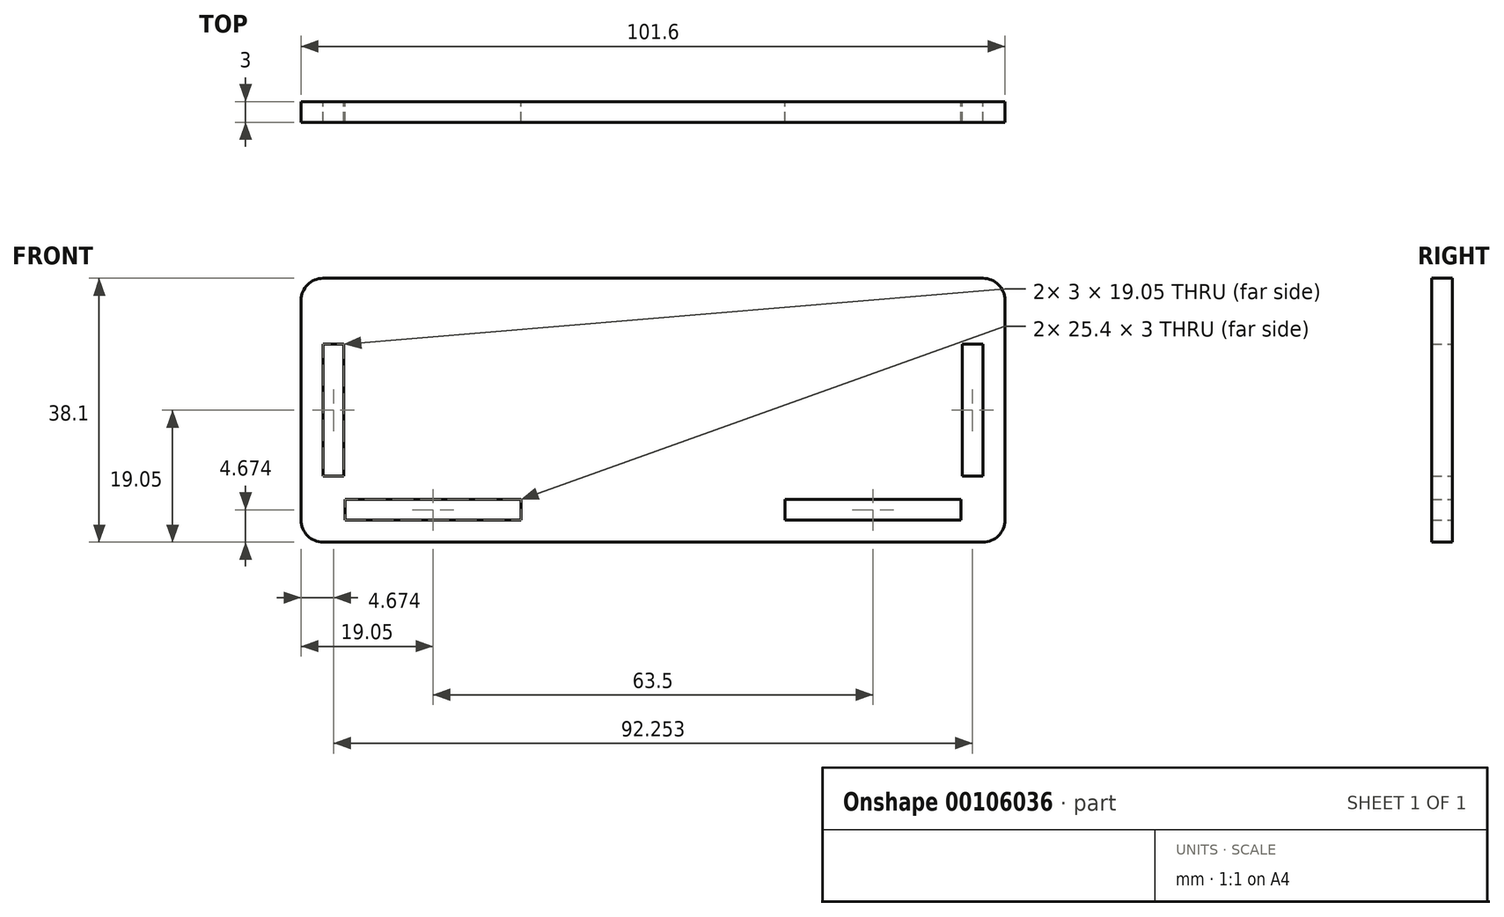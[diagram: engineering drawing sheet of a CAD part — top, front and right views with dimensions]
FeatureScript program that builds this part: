
annotation { "Feature Type Name" : "Feature", "Feature Type Description" : "" }
export const myFeature = defineFeature(function(context is Context, id is Id, definition is map)
    precondition{}
    {
        {
            var Q0;
            Q0=qCreatedBy(makeId("Front.planeOp"),FACE);
            var sketch = newSketch(context, id + "F0", { "sketchPlane" : qUnion([Q0])});
            skLineSegment(sketch, "E0.bottom", {"start": v(-47.63, 0) * mm, "end": v(47.63, 0) * mm});
            skLineSegment(sketch, "E0.top", {"start": v(-47.63, 38.1) * mm, "end": v(47.63, 38.1) * mm});
            skLineSegment(sketch, "E0.left", {"start": v(-50.8, 3.18) * mm, "end": v(-50.8, 34.92) * mm});
            skLineSegment(sketch, "E0.right", {"start": v(50.8, 3.18) * mm, "end": v(50.8, 34.93) * mm});
            skLineSegment(sketch, "E1.bottom", {"start": v(-44.45, 3.17) * mm, "end": v(-19.05, 3.17) * mm});
            skLineSegment(sketch, "E1.top", {"start": v(-44.45, 6.17) * mm, "end": v(-19.05, 6.17) * mm});
            skLineSegment(sketch, "E1.left", {"start": v(-44.45, 3.17) * mm, "end": v(-44.45, 6.17) * mm});
            skLineSegment(sketch, "E1.right", {"start": v(-19.05, 3.17) * mm, "end": v(-19.05, 6.17) * mm});
            skLineSegment(sketch, "E2.bottom", {"start": v(19.05, 3.17) * mm, "end": v(44.45, 3.17) * mm});
            skLineSegment(sketch, "E2.top", {"start": v(19.05, 6.17) * mm, "end": v(44.45, 6.17) * mm});
            skLineSegment(sketch, "E2.left", {"start": v(19.05, 3.17) * mm, "end": v(19.05, 6.17) * mm});
            skLineSegment(sketch, "E2.right", {"start": v(44.45, 3.17) * mm, "end": v(44.45, 6.17) * mm});
            skLineSegment(sketch, "E3.bottom", {"start": v(-44.63, 28.57) * mm, "end": v(-47.62, 28.57) * mm});
            skLineSegment(sketch, "E3.top", {"start": v(-44.63, 9.53) * mm, "end": v(-47.62, 9.53) * mm});
            skLineSegment(sketch, "E3.left", {"start": v(-44.63, 28.57) * mm, "end": v(-44.63, 9.52) * mm});
            skLineSegment(sketch, "E3.right", {"start": v(-47.63, 28.57) * mm, "end": v(-47.63, 9.53) * mm});
            skLineSegment(sketch, "E4.bottom", {"start": v(47.62, 28.57) * mm, "end": v(44.63, 28.57) * mm});
            skLineSegment(sketch, "E4.top", {"start": v(47.62, 9.52) * mm, "end": v(44.63, 9.52) * mm});
            skLineSegment(sketch, "E4.left", {"start": v(47.63, 28.57) * mm, "end": v(47.63, 9.52) * mm});
            skLineSegment(sketch, "E4.right", {"start": v(44.63, 28.58) * mm, "end": v(44.63, 9.53) * mm});
            skPoint(sketch, "E5.visualSharp", {"position": v(-50.8, 38.1) * mm});
            skArc(sketch, "E5.filletArc", {"start": v(-47.63, 38.1) * mm, "mid": v(-49.87, 37.17) * mm, "end": v(-50.8, 34.92) * mm});
            skPoint(sketch, "E6.visualSharp", {"position": v(50.8, 38.1) * mm});
            skArc(sketch, "E6.filletArc", {"start": v(50.8, 34.93) * mm, "mid": v(49.87, 37.17) * mm, "end": v(47.63, 38.1) * mm});
            skPoint(sketch, "E7.visualSharp", {"position": v(-50.8, 0) * mm});
            skArc(sketch, "E7.filletArc", {"start": v(-50.8, 3.17) * mm, "mid": v(-49.87, 0.93) * mm, "end": v(-47.63, 0) * mm});
            skPoint(sketch, "E8.visualSharp", {"position": v(50.8, 0) * mm});
            skArc(sketch, "E8.filletArc", {"start": v(47.63, 0) * mm, "mid": v(49.87, 0.93) * mm, "end": v(50.8, 3.18) * mm});
            skSolve(sketch);
        }
        {
            var Q0;
            Q0=makeQuery(id+"F0.imprint","IMPRINT",FACE,{"disambiguationData":[TD([[makeQuery(id+"F0.imprint","IMPRINT",EDGE,{"derivedFrom":sQuery(id+"F0.wireOp",EDGE,"E0.bottom")}),1.0]])]});
            extrude(context, id + "F1", {"entities" : qUnion([Q0]), "depth" : 3 * mm});
        }
    });
